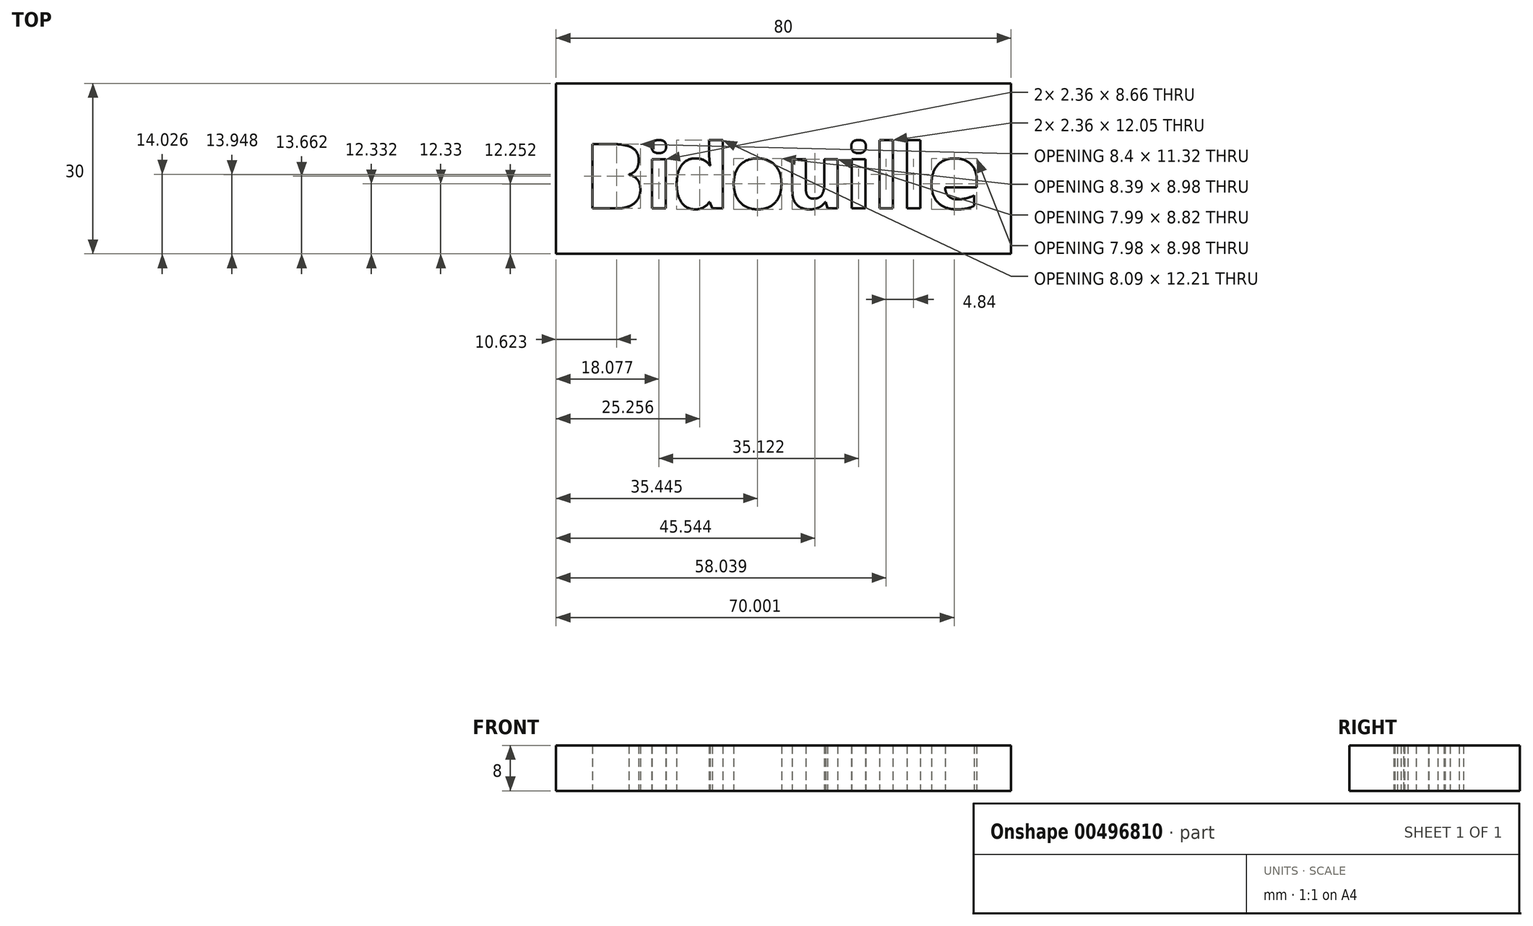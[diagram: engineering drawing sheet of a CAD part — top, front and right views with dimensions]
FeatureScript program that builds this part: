
annotation { "Feature Type Name" : "Feature", "Feature Type Description" : "" }
export const myFeature = defineFeature(function(context is Context, id is Id, definition is map)
    precondition{}
    {
        {
            var Q0;
            Q0=qCreatedBy(makeId("Top.planeOp"),FACE);
            var sketch = newSketch(context, id + "F0", { "sketchPlane" : qUnion([Q0])});
            skLineSegment(sketch, "E0.bottom", {"start": v(-35.67, -2.69) * mm, "end": v(44.33, -2.69) * mm});
            skLineSegment(sketch, "E0.top", {"start": v(-35.67, -32.69) * mm, "end": v(44.33, -32.69) * mm});
            skLineSegment(sketch, "E0.left", {"start": v(-35.67, -2.69) * mm, "end": v(-35.67, -32.69) * mm});
            skLineSegment(sketch, "E0.right", {"start": v(44.33, -2.69) * mm, "end": v(44.33, -32.69) * mm});
            skText(sketch, "E1", { "text": "Bidouille", "fontName": "OpenSans-Bold.ttf"});
            const initialGuessF0  = {"E1": [-0.03067, -0.02469, 1, 0, 0.01142]};
            skSetInitialGuess(sketch, initialGuessF0);
            skSolve(sketch);
        }
        {
            var Q0;
            Q0=makeQuery(id+"F0.imprint","IMPRINT",FACE,{"disambiguationData":[TD([[makeQuery(id+"F0.imprint","IMPRINT",EDGE,{"derivedFrom":sQuery(id+"F0.wireOp",EDGE,"E0.bottom")}),-1.0]])]});
            extrude(context, id + "F1", {"entities" : qUnion([Q0]), "depth" : 8 * mm});
        }
    });
